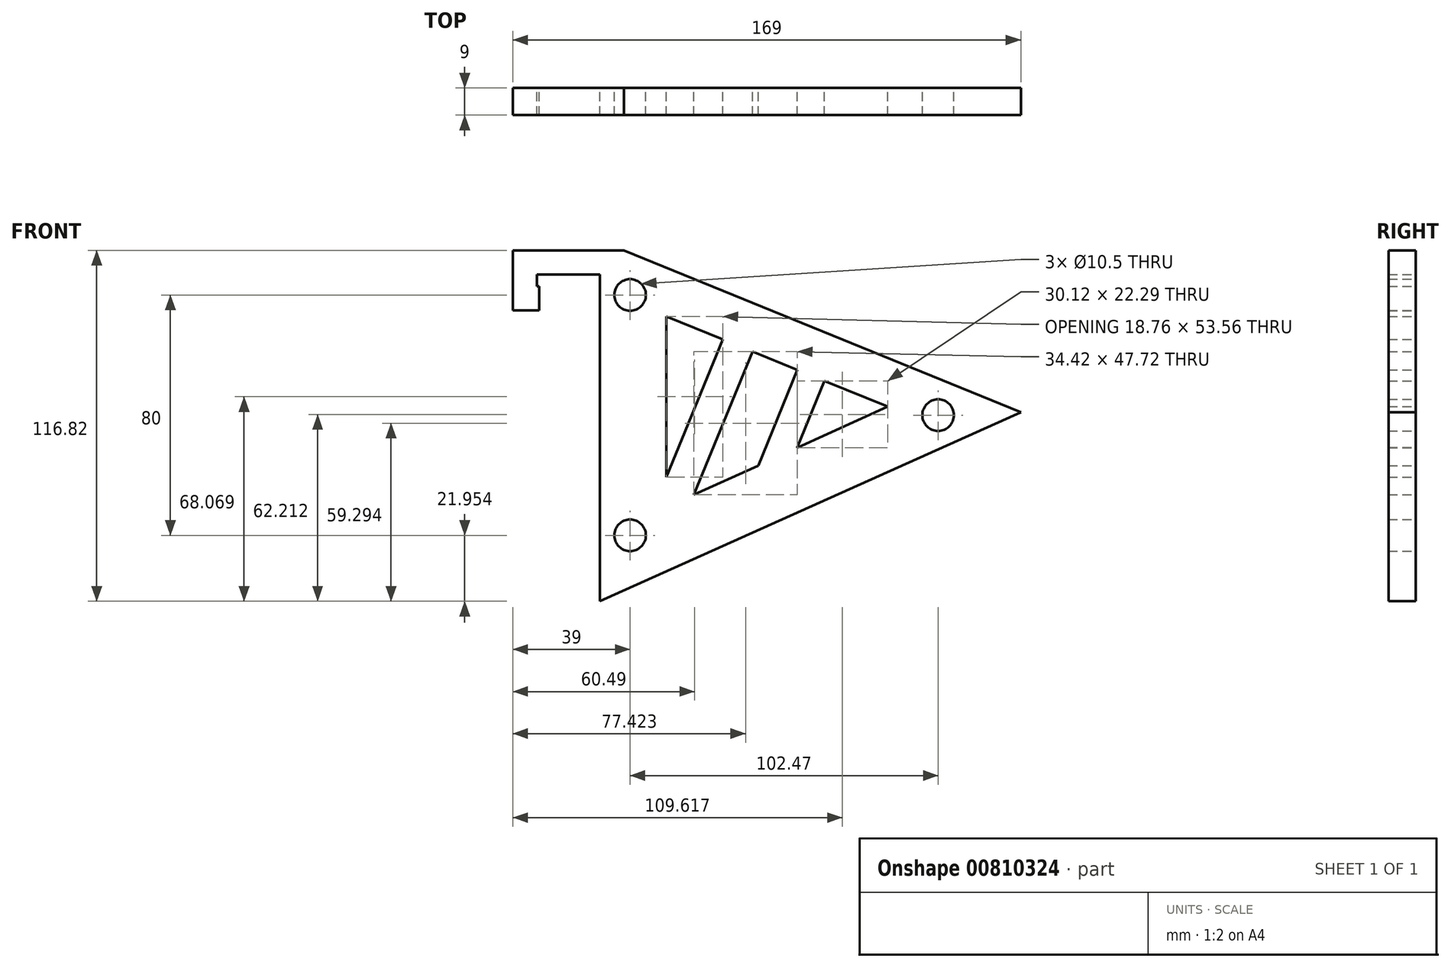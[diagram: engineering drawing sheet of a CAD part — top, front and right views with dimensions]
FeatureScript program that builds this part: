
annotation { "Feature Type Name" : "Feature", "Feature Type Description" : "" }
export const myFeature = defineFeature(function(context is Context, id is Id, definition is map)
    precondition{}
    {
        {
            var Q0;
            Q0=qCreatedBy(makeId("Front.planeOp"),FACE);
            var sketch = newSketch(context, id + "F0", { "sketchPlane" : qUnion([Q0])});
            skLineSegment(sketch, "E0", {"start": v(21, 0) * mm, "end": v(29, 0) * mm});
            skLineSegment(sketch, "E1", {"start": v(21, 0) * mm, "end": v(21, -109.63) * mm});
            skCircle(sketch, "E2", {"center": v(31, -94.87) * mm, "radius": 5.25 * mm});
            skCircle(sketch, "E3", {"center": v(31, -14.87) * mm, "radius": 5.25 * mm});
            skCircle(sketch, "E4", {"center": v(133.47, -54.87) * mm, "radius": 5.25 * mm});
            skLineSegment(sketch, "E5", {"start": v(29, 0) * mm, "end": v(161, -53.96) * mm});
            skLineSegment(sketch, "E6", {"start": v(21, -144.17) * mm, "end": v(21, -109.63) * mm});
            skLineSegment(sketch, "E7", {"start": v(43.11, -21.97) * mm, "end": v(116.68, -52.05) * mm});
            skLineSegment(sketch, "E8", {"start": v(43.11, -85.53) * mm, "end": v(43.11, -21.97) * mm});
            skLineSegment(sketch, "E9", {"start": v(116.68, -52.05) * mm, "end": v(119.96, -50.55) * mm});
            skLineSegment(sketch, "E10", {"start": v(119.96, -50.55) * mm, "end": v(43.11, -85.53) * mm});
            skLineSegment(sketch, "E11", {"start": v(61.87, -29.64) * mm, "end": v(43.11, -75.53) * mm});
            skLineSegment(sketch, "E12", {"start": v(71.72, -33.67) * mm, "end": v(52.21, -81.39) * mm});
            skLineSegment(sketch, "E13", {"start": v(161, -53.96) * mm, "end": v(21, -116.82) * mm});
            skLineSegment(sketch, "E14", {"start": v(21, -8) * mm, "end": v(0, -8) * mm});
            skLineSegment(sketch, "E15", {"start": v(0, -8) * mm, "end": v(0, -20) * mm});
            skLineSegment(sketch, "E16", {"start": v(0, -20) * mm, "end": v(-8, -20) * mm});
            skLineSegment(sketch, "E17", {"start": v(-8, -20) * mm, "end": v(-8, 0) * mm});
            skLineSegment(sketch, "E18", {"start": v(-8, 0) * mm, "end": v(21, 0) * mm});
            skLineSegment(sketch, "E19", {"start": v(0, -12) * mm, "end": v(0.75, -12) * mm});
            skLineSegment(sketch, "E20", {"start": v(0, -20) * mm, "end": v(0.75, -20) * mm});
            skLineSegment(sketch, "E21", {"start": v(0.75, -12) * mm, "end": v(0.75, -20) * mm});
            skLineSegment(sketch, "E22", {"start": v(86.63, -39.76) * mm, "end": v(73.6, -71.65) * mm});
            skLineSegment(sketch, "E23", {"start": v(95.68, -43.46) * mm, "end": v(92.87, -50.33) * mm});
            skLineSegment(sketch, "E24", {"start": v(92.87, -50.33) * mm, "end": v(86.63, -65.6) * mm});
            skLineSegment(sketch, "E25", {"start": v(86.63, -65.6) * mm, "end": v(86.56, -65.75) * mm});
            skSolve(sketch);
        }
        {
            var Q0;
            {var subQ0=sQuery(id+"F0.wireOp",EDGE,"iasNVvJb-WD1q-CJzO-sZDG-wx9UWVCc2D5B");Q0=makeQuery(id+"F0.imprint","IMPRINT",FACE,{"disambiguationData":[TD([[makeQuery(id+"F0.imprint","IMPRINT",EDGE,{"derivedFrom":subQ0}),1.0]])]});}
            var Q1;
            {var subQ2=sQuery(id+"F0.wireOp",EDGE,"caxPJMYp-jc2R-sr8P-LCId-3kQJVGewICNK");Q1=makeQuery(id+"F0.imprint","IMPRINT",FACE,{"disambiguationData":[TD([[makeQuery(id+"F0.imprint","IMPRINT",EDGE,{"derivedFrom":subQ2}),-1.0]])]});}
            var Q2;
            Q2=makeQuery(id+"F0.imprint","IMPRINT",FACE,{"disambiguationData":[TD([[makeQuery(id+"F0.imprint","IMPRINT",EDGE,{"derivedFrom":sQuery(id+"F0.wireOp",EDGE,"E0")}),-1.0]])]});
            var Q3;
            {var subQ0=sQuery(id+"F0.wireOp",EDGE,"E11");Q3=makeQuery(id+"F0.imprint","IMPRINT",FACE,{"disambiguationData":[TD([[makeQuery(id+"F0.imprint","IMPRINT",EDGE,{"derivedFrom":subQ0}),1.0]])]});}
            var Q4;
            {var subQ3=sQuery(id+"F0.wireOp",EDGE,"E14");Q4=makeQuery(id+"F0.imprint","IMPRINT",FACE,{"disambiguationData":[TD([[makeQuery(id+"F0.imprint","IMPRINT",EDGE,{"derivedFrom":subQ3}),-1.0]])]});}
            var Q5;
            {var subQ2=sQuery(id+"F0.wireOp",EDGE,"E19");Q5=makeQuery(id+"F0.imprint","IMPRINT",FACE,{"disambiguationData":[TD([[makeQuery(id+"F0.imprint","IMPRINT",EDGE,{"derivedFrom":subQ2}),-1.0]])]});}
            var Q6;
            {var subQ1=sQuery(id+"F0.wireOp",EDGE,"E22");Q6=makeQuery(id+"F0.imprint","IMPRINT",FACE,{"disambiguationData":[TD([[makeQuery(id+"F0.imprint","IMPRINT",EDGE,{"derivedFrom":subQ1}),1.0]])]});}
            extrude(context, id + "F1", {"entities" : qUnion([Q0, Q1, Q2, Q3, Q4, Q5, Q6]), "depth" : 9 * mm, "offsetDistance" : 25 * mm});
        }
    });
